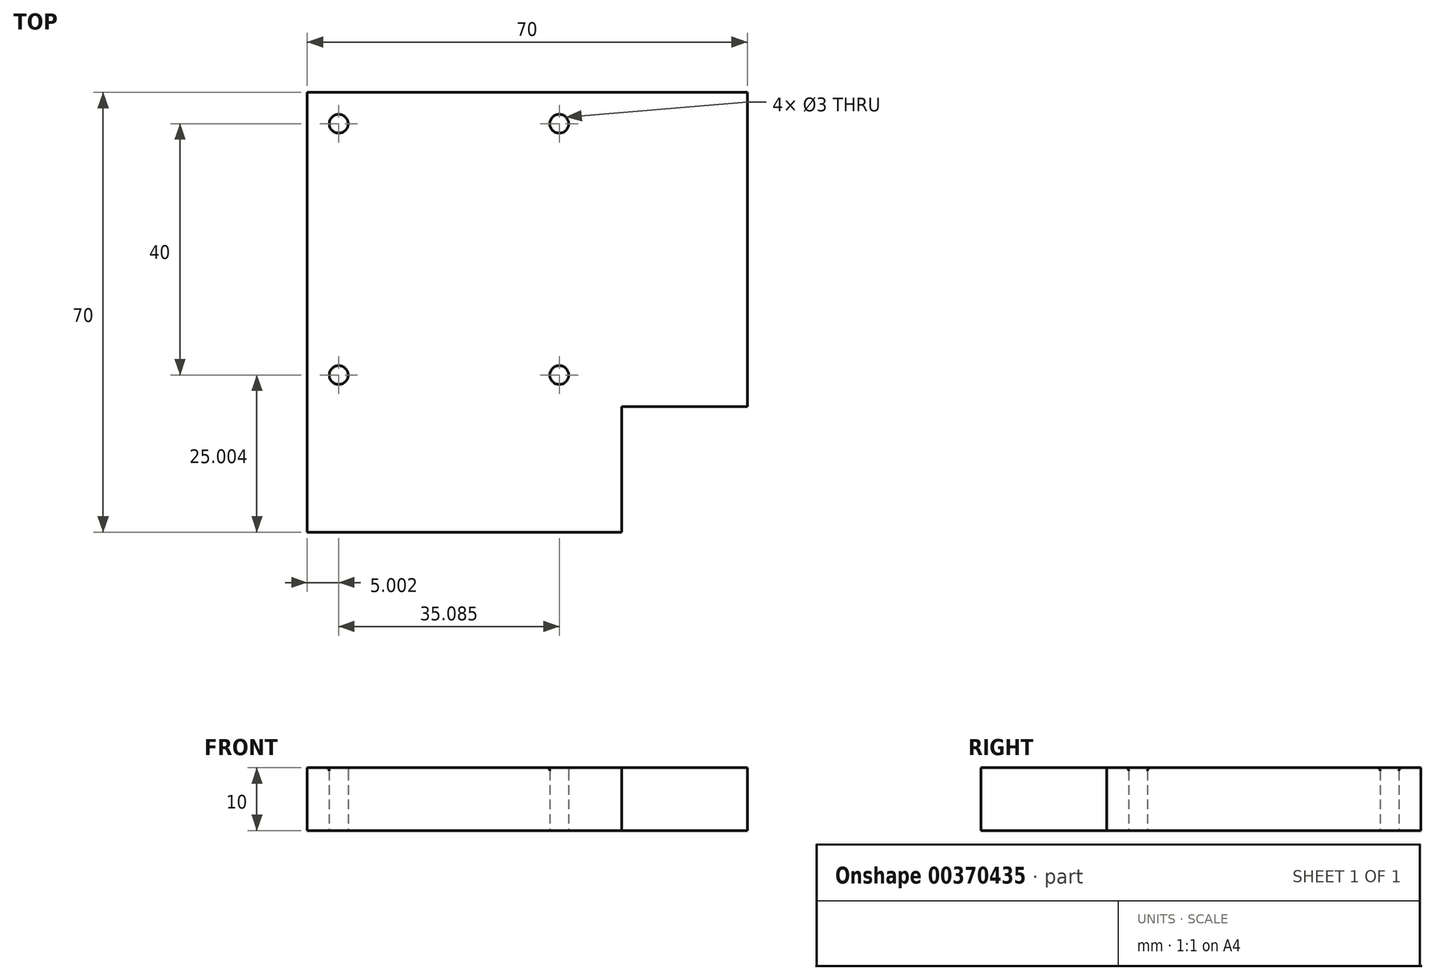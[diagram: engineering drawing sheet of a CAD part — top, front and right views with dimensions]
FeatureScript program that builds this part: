
annotation { "Feature Type Name" : "Feature", "Feature Type Description" : "" }
export const myFeature = defineFeature(function(context is Context, id is Id, definition is map)
    precondition{}
    {
        {
            var Q0;
            Q0=qCreatedBy(makeId("Top.planeOp"),FACE);
            var sketch = newSketch(context, id + "F0", { "sketchPlane" : qUnion([Q0])});
            skLineSegment(sketch, "E0", {"start": v(-28.8, 61.5) * mm, "end": v(41.2, 61.5) * mm});
            skLineSegment(sketch, "E1", {"start": v(41.2, 61.5) * mm, "end": v(41.2, 11.5) * mm});
            skLineSegment(sketch, "E2", {"start": v(41.2, 11.5) * mm, "end": v(21.2, 11.5) * mm});
            skLineSegment(sketch, "E3", {"start": v(21.2, 11.5) * mm, "end": v(21.2, -8.5) * mm});
            skLineSegment(sketch, "E4", {"start": v(-28.8, 61.5) * mm, "end": v(-28.8, -8.5) * mm});
            skLineSegment(sketch, "E5", {"start": v(-28.8, -8.5) * mm, "end": v(21.2, -8.5) * mm});
            skSolve(sketch);
        }
        {
            var Q0;
            Q0 = qSketchRegion(id + "F0", true);
            extrude(context, id + "F1", {"entities" : qUnion([Q0]), "depth" : 10 * mm});
        }
        {
            var Q0;
            Q0=qCreatedBy(makeId("Top.planeOp"),FACE);
            var sketch = newSketch(context, id + "F2", { "sketchPlane" : qUnion([Q0])});
            skCircle(sketch, "E6", {"center": v(-23.8, 56.5) * mm, "radius": 1.5 * mm});
            skCircle(sketch, "E7", {"center": v(11.28, 56.5) * mm, "radius": 1.5 * mm});
            skCircle(sketch, "E8", {"center": v(11.28, 16.5) * mm, "radius": 1.5 * mm});
            skCircle(sketch, "E9", {"center": v(-23.8, 16.5) * mm, "radius": 1.5 * mm});
            skSolve(sketch);
        }
        {
            var Q0;
            Q0 = qSketchRegion(id + "F2", true);
            extrude(context, id + "F3", {"entities" : qUnion([Q0]), "operationType" : NewBodyOperationType.REMOVE, "endBound" : BoundingType.THROUGH_ALL, "depth" : 25 * mm});
        }
        {
            var Q0;
            Q0=makeQuery(id+"F3.boolean.opBoolean","INTERSECT",EDGE,{"derivedFrom":[makeQuery(id+"F1.opExtrude","CAP_FACE",FACE,{"disambiguationData":[OSD([sQuery(id+"F0.wireOp",EDGE,"E0"),sQuery(id+"F0.wireOp",EDGE,"E1"),sQuery(id+"F0.wireOp",EDGE,"E2"),sQuery(id+"F0.wireOp",EDGE,"E3"),sQuery(id+"F0.wireOp",EDGE,"E4"),sQuery(id+"F0.wireOp",EDGE,"E5")])],"isStart":false}),makeQuery(id+"F3.opExtrude","SWEPT_FACE",FACE,{"disambiguationData":[OSD([sQuery(id+"F2.wireOp",EDGE,"E9")])]})]});
            var Q1;
            Q1=makeQuery(id+"F3.boolean.opBoolean","INTERSECT",EDGE,{"derivedFrom":[makeQuery(id+"F1.opExtrude","CAP_FACE",FACE,{"disambiguationData":[OSD([sQuery(id+"F0.wireOp",EDGE,"E0"),sQuery(id+"F0.wireOp",EDGE,"E1"),sQuery(id+"F0.wireOp",EDGE,"E2"),sQuery(id+"F0.wireOp",EDGE,"E3"),sQuery(id+"F0.wireOp",EDGE,"E4"),sQuery(id+"F0.wireOp",EDGE,"E5")])],"isStart":false}),makeQuery(id+"F3.opExtrude","SWEPT_FACE",FACE,{"disambiguationData":[OSD([sQuery(id+"F2.wireOp",EDGE,"E6")])]})]});
            var Q2;
            Q2=makeQuery(id+"F3.boolean.opBoolean","INTERSECT",EDGE,{"derivedFrom":[makeQuery(id+"F1.opExtrude","CAP_FACE",FACE,{"disambiguationData":[OSD([sQuery(id+"F0.wireOp",EDGE,"E0"),sQuery(id+"F0.wireOp",EDGE,"E1"),sQuery(id+"F0.wireOp",EDGE,"E2"),sQuery(id+"F0.wireOp",EDGE,"E3"),sQuery(id+"F0.wireOp",EDGE,"E4"),sQuery(id+"F0.wireOp",EDGE,"E5")])],"isStart":false}),makeQuery(id+"F3.opExtrude","SWEPT_FACE",FACE,{"disambiguationData":[OSD([sQuery(id+"F2.wireOp",EDGE,"E7")])]})]});
            var Q3;
            Q3=makeQuery(id+"F3.boolean.opBoolean","INTERSECT",EDGE,{"derivedFrom":[makeQuery(id+"F1.opExtrude","CAP_FACE",FACE,{"disambiguationData":[OSD([sQuery(id+"F0.wireOp",EDGE,"E0"),sQuery(id+"F0.wireOp",EDGE,"E1"),sQuery(id+"F0.wireOp",EDGE,"E2"),sQuery(id+"F0.wireOp",EDGE,"E3"),sQuery(id+"F0.wireOp",EDGE,"E4"),sQuery(id+"F0.wireOp",EDGE,"E5")])],"isStart":false}),makeQuery(id+"F3.opExtrude","SWEPT_FACE",FACE,{"disambiguationData":[OSD([sQuery(id+"F2.wireOp",EDGE,"E8")])]})]});
            fillet(context, id + "F4", {"entities" : qUnion([Q0, Q1, Q2, Q3]), "radius" : 0.5 * mm, "tangentPropagation" : true, "allowEdgeOverflow" : false});
        }
    });
